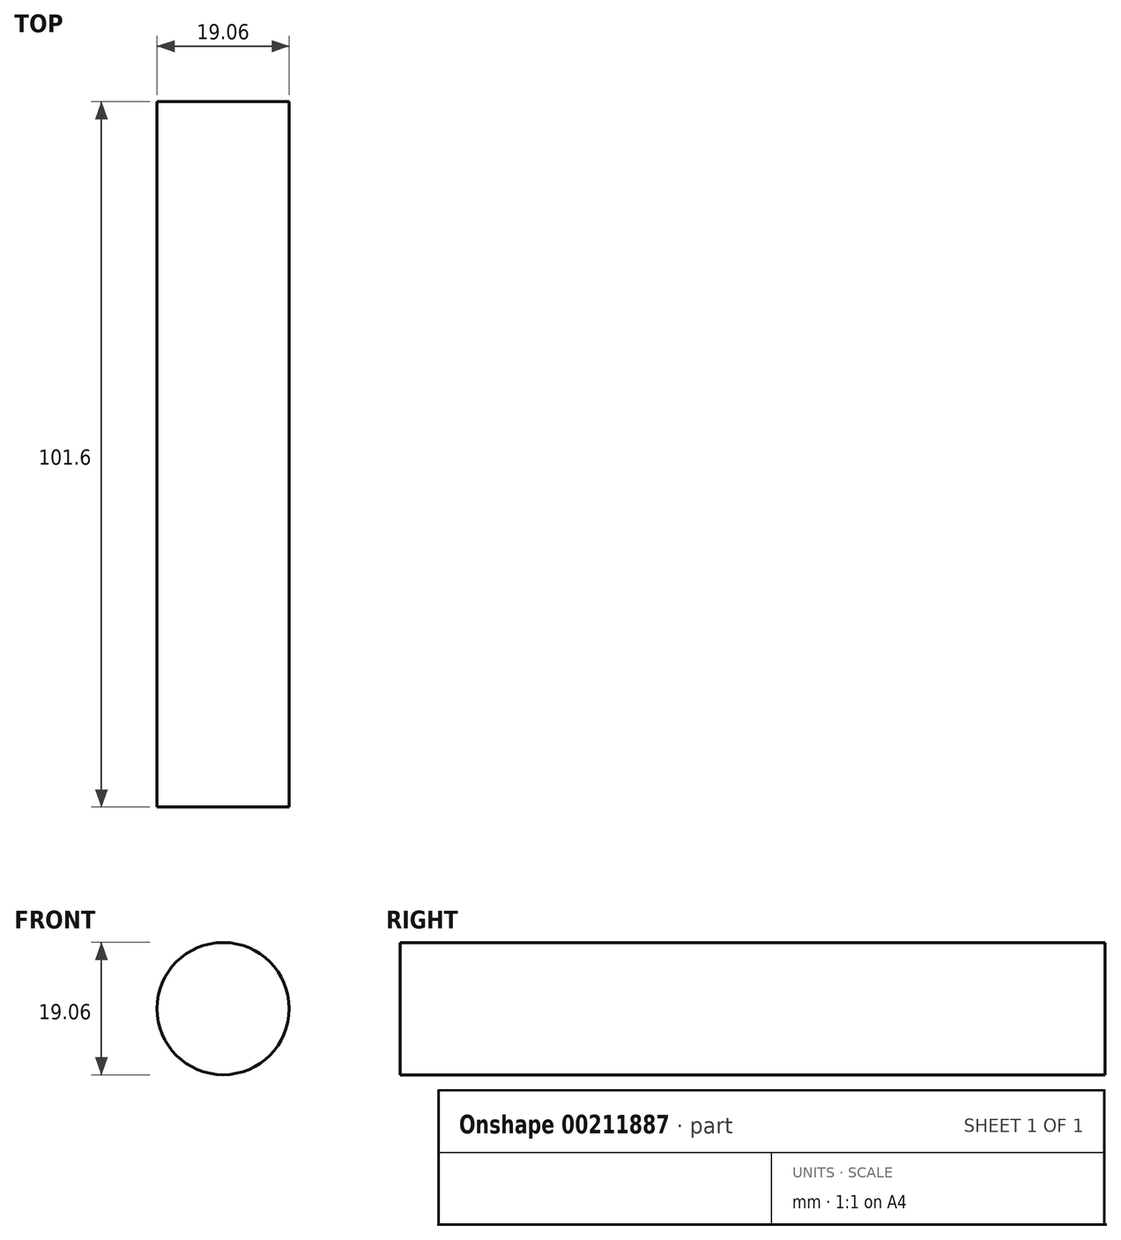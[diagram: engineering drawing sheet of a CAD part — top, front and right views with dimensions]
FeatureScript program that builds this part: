
annotation { "Feature Type Name" : "Feature", "Feature Type Description" : "" }
export const myFeature = defineFeature(function(context is Context, id is Id, definition is map)
    precondition{}
    {
        {
            var Q0;
            Q0=qCreatedBy(makeId("Front.planeOp"),FACE);
            var sketch = newSketch(context, id + "F0", { "sketchPlane" : qUnion([Q0])});
            skCircle(sketch, "E0", {"center": v(0, 0) * mm, "radius": 9.53 * mm});
            skSolve(sketch);
        }
        {
            var Q0;
            Q0 = qSketchRegion(id + "F0", true);
            extrude(context, id + "F1", {"entities" : qUnion([Q0]), "endBound" : BoundingType.SYMMETRIC, "depth" : 101.6 * mm});
        }
    });
